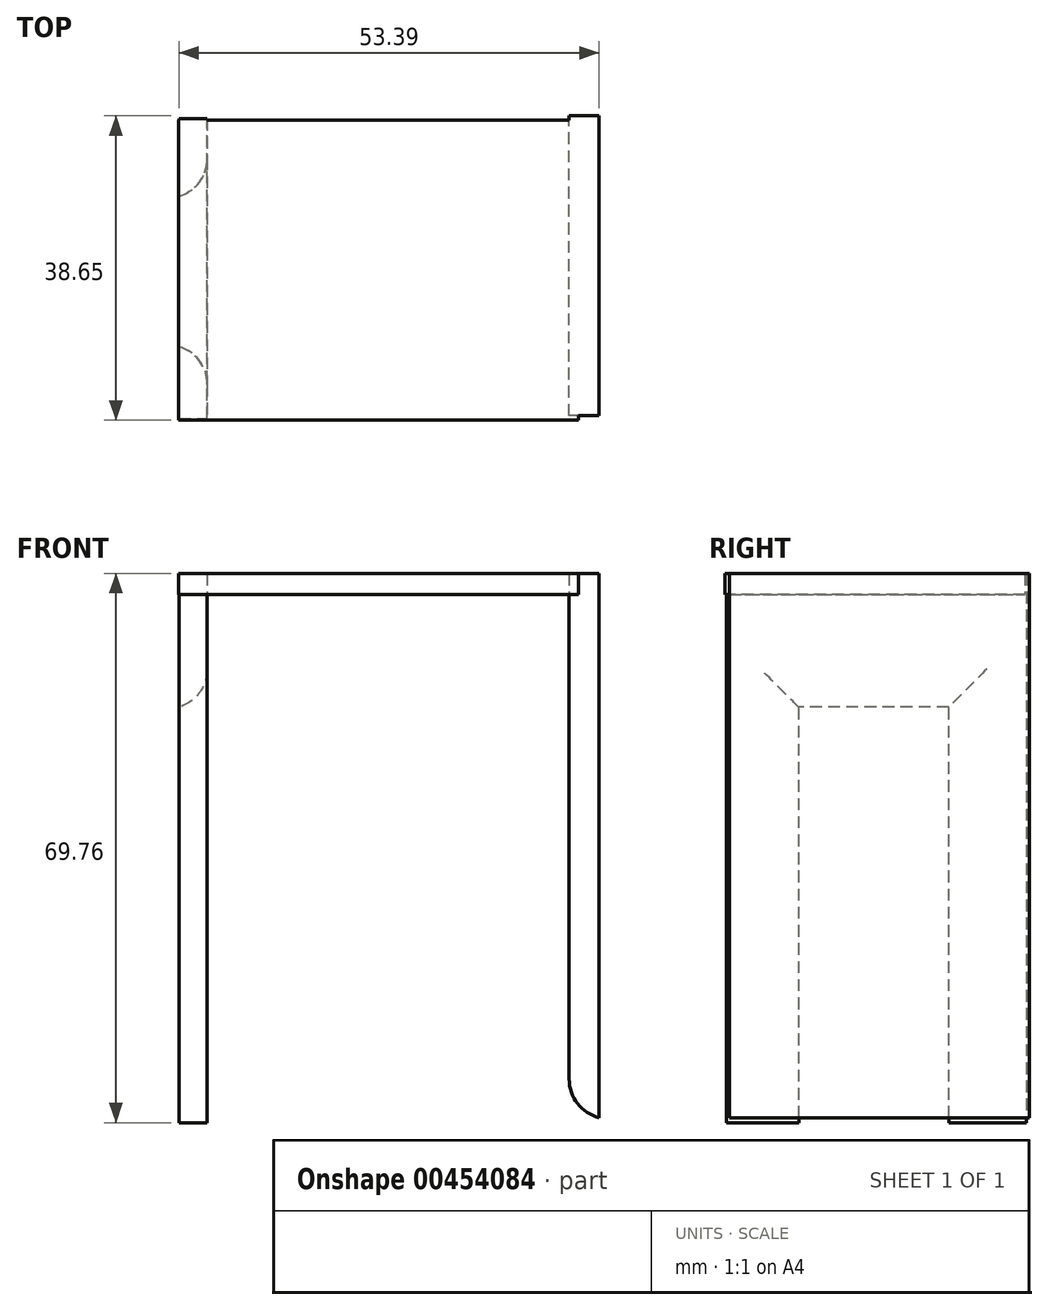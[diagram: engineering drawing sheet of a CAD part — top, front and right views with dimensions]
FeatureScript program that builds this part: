
annotation { "Feature Type Name" : "Feature", "Feature Type Description" : "" }
export const myFeature = defineFeature(function(context is Context, id is Id, definition is map)
    precondition{}
    {
        {
            var Q0;
            Q0=qCreatedBy(makeId("Top.planeOp"),FACE);
            var sketch = newSketch(context, id + "F0", { "sketchPlane" : qUnion([Q0])});
            skLineSegment(sketch, "E0.bottom", {"start": v(-21.9, 25.72) * mm, "end": v(28.9, 25.72) * mm});
            skLineSegment(sketch, "E0.top", {"start": v(-21.9, -12.38) * mm, "end": v(28.9, -12.38) * mm});
            skLineSegment(sketch, "E0.left", {"start": v(-21.9, 25.72) * mm, "end": v(-21.9, -12.38) * mm});
            skLineSegment(sketch, "E0.right", {"start": v(28.9, 25.72) * mm, "end": v(28.9, -12.38) * mm});
            skSolve(sketch);
        }
        {
            var Q0;
            Q0 = qSketchRegion(id + "F0", true);
            extrude(context, id + "F1", {"entities" : qUnion([Q0]), "depth" : 3.17 * mm});
        }
        {
            var Q0;
            Q0=qCreatedBy(makeId("Right.planeOp"),FACE);
            var sketch = newSketch(context, id + "F2", { "sketchPlane" : qUnion([Q0])});
            skLineSegment(sketch, "E1.bottom", {"start": v(25.9, 2.76) * mm, "end": v(-12.2, 2.76) * mm});
            skLineSegment(sketch, "E1.top", {"start": v(25.9, -67.1) * mm, "end": v(-12.2, -67.1) * mm});
            skLineSegment(sketch, "E1.left", {"start": v(25.9, 2.76) * mm, "end": v(25.9, -67.1) * mm});
            skLineSegment(sketch, "E1.right", {"start": v(-12.2, 2.76) * mm, "end": v(-12.2, -67.1) * mm});
            skSolve(sketch);
        }
        {
            var Q0;
            Q0 = qSketchRegion(id + "F2", true);
            extrude(context, id + "F3", {"entities" : qUnion([Q0]), "operationType" : NewBodyOperationType.ADD, "oppositeDirection" : true, "depth" : 21.84 * mm, "hasSecondDirection" : true, "secondDirectionOppositeDirection" : true, "secondDirectionDepth" : 18.29 * mm});
        }
        {
            var Q0;
            Q0=qCreatedBy(makeId("Right.planeOp"),FACE);
            var sketch = newSketch(context, id + "F4", { "sketchPlane" : qUnion([Q0])});
            skLineSegment(sketch, "E2.bottom", {"start": v(26.27, 3.37) * mm, "end": v(-11.83, 3.37) * mm});
            skLineSegment(sketch, "E2.top", {"start": v(26.27, -66.48) * mm, "end": v(-11.83, -66.48) * mm});
            skLineSegment(sketch, "E2.left", {"start": v(26.27, 3.37) * mm, "end": v(26.27, -66.48) * mm});
            skLineSegment(sketch, "E2.right", {"start": v(-11.83, 3.37) * mm, "end": v(-11.83, -66.48) * mm});
            skSolve(sketch);
        }
        {
            var Q0;
            Q0 = qSketchRegion(id + "F4", true);
            extrude(context, id + "F5", {"entities" : qUnion([Q0]), "operationType" : NewBodyOperationType.ADD, "depth" : 31.5 * mm, "hasSecondDirection" : true, "secondDirectionOppositeDirection" : false, "secondDirectionDepth" : 27.7 * mm});
        }
        {
            var Q0;
            Q0=qCreatedBy(makeId("Right.planeOp"),FACE);
            var sketch = newSketch(context, id + "F6", { "sketchPlane" : qUnion([Q0])});
            skLineSegment(sketch, "E3.bottom", {"start": v(16.02, -68.28) * mm, "end": v(-3.03, -68.28) * mm});
            skLineSegment(sketch, "E3.top", {"start": v(16.02, -14.3) * mm, "end": v(-3.03, -14.3) * mm});
            skLineSegment(sketch, "E3.left", {"start": v(16.02, -68.28) * mm, "end": v(16.02, -14.3) * mm});
            skLineSegment(sketch, "E3.right", {"start": v(-3.03, -68.28) * mm, "end": v(-3.03, -14.3) * mm});
            skSolve(sketch);
        }
        {
            var Q0;
            Q0 = qSketchRegion(id + "F6", true);
            extrude(context, id + "F7", {"entities" : qUnion([Q0]), "operationType" : NewBodyOperationType.REMOVE, "oppositeDirection" : true, "depth" : 32 * mm});
        }
        {
            var Q0;
            Q0=makeQuery(id+"F7.boolean.opBoolean","INTERSECT",EDGE,{"derivedFrom":[makeQuery(id+"F3.opExtrude","CAP_FACE",FACE,{"disambiguationData":[OSD([sQuery(id+"F2.wireOp",EDGE,"E1.bottom"),sQuery(id+"F2.wireOp",EDGE,"E1.top"),sQuery(id+"F2.wireOp",EDGE,"E1.left"),sQuery(id+"F2.wireOp",EDGE,"E1.right")])],"isStart":true}),makeQuery(id+"F7.opExtrude","SWEPT_FACE",FACE,{"disambiguationData":[OSD([sQuery(id+"F6.wireOp",EDGE,"E3.left")])]})]});
            var Q1;
            Q1=makeQuery(id+"F7.boolean.opBoolean","INTERSECT",EDGE,{"derivedFrom":[makeQuery(id+"F3.opExtrude","CAP_FACE",FACE,{"disambiguationData":[OSD([sQuery(id+"F2.wireOp",EDGE,"E1.bottom"),sQuery(id+"F2.wireOp",EDGE,"E1.top"),sQuery(id+"F2.wireOp",EDGE,"E1.left"),sQuery(id+"F2.wireOp",EDGE,"E1.right")])],"isStart":true}),makeQuery(id+"F7.opExtrude","SWEPT_FACE",FACE,{"disambiguationData":[OSD([sQuery(id+"F6.wireOp",EDGE,"E3.top")])]})]});
            var Q2;
            Q2=makeQuery(id+"F7.boolean.opBoolean","INTERSECT",EDGE,{"derivedFrom":[makeQuery(id+"F3.opExtrude","CAP_FACE",FACE,{"disambiguationData":[OSD([sQuery(id+"F2.wireOp",EDGE,"E1.bottom"),sQuery(id+"F2.wireOp",EDGE,"E1.top"),sQuery(id+"F2.wireOp",EDGE,"E1.left"),sQuery(id+"F2.wireOp",EDGE,"E1.right")])],"isStart":true}),makeQuery(id+"F7.opExtrude","SWEPT_FACE",FACE,{"disambiguationData":[OSD([sQuery(id+"F6.wireOp",EDGE,"E3.right")])]})]});
            var Q3;
            Q3=makeQuery(id+"F5.opExtrude","CAP_EDGE",EDGE,{"disambiguationData":[OSD([sQuery(id+"F4.wireOp",EDGE,"E2.top")])],"isStart":true});
            fillet(context, id + "F8", {"entities" : qUnion([Q0, Q1, Q2, Q3]), "radius" : 5.08 * mm, "tangentPropagation" : true, "allowEdgeOverflow" : false});
        }
        {
            var Q0;
            Q0=qCreatedBy(makeId("Front.planeOp"),FACE);
            var sketch = newSketch(context, id + "F9", { "sketchPlane" : qUnion([Q0])});
            skLineSegment(sketch, "E4.bottom", {"start": v(-22.82, 4.16) * mm, "end": v(32.1, 4.16) * mm});
            skLineSegment(sketch, "E4.top", {"start": v(-22.82, 2.67) * mm, "end": v(32.1, 2.67) * mm});
            skLineSegment(sketch, "E4.left", {"start": v(-22.82, 4.16) * mm, "end": v(-22.82, 2.67) * mm});
            skLineSegment(sketch, "E4.right", {"start": v(32.1, 4.16) * mm, "end": v(32.1, 2.67) * mm});
            skSolve(sketch);
        }
        {
            var Q0;
            Q0 = qSketchRegion(id + "F9", true);
            extrude(context, id + "F10", {"entities" : qUnion([Q0]), "operationType" : NewBodyOperationType.REMOVE, "oppositeDirection" : true, "depth" : 28.5 * mm, "hasSecondDirection" : true, "secondDirectionOppositeDirection" : false, "secondDirectionDepth" : 25.4 * mm});
        }
    });
